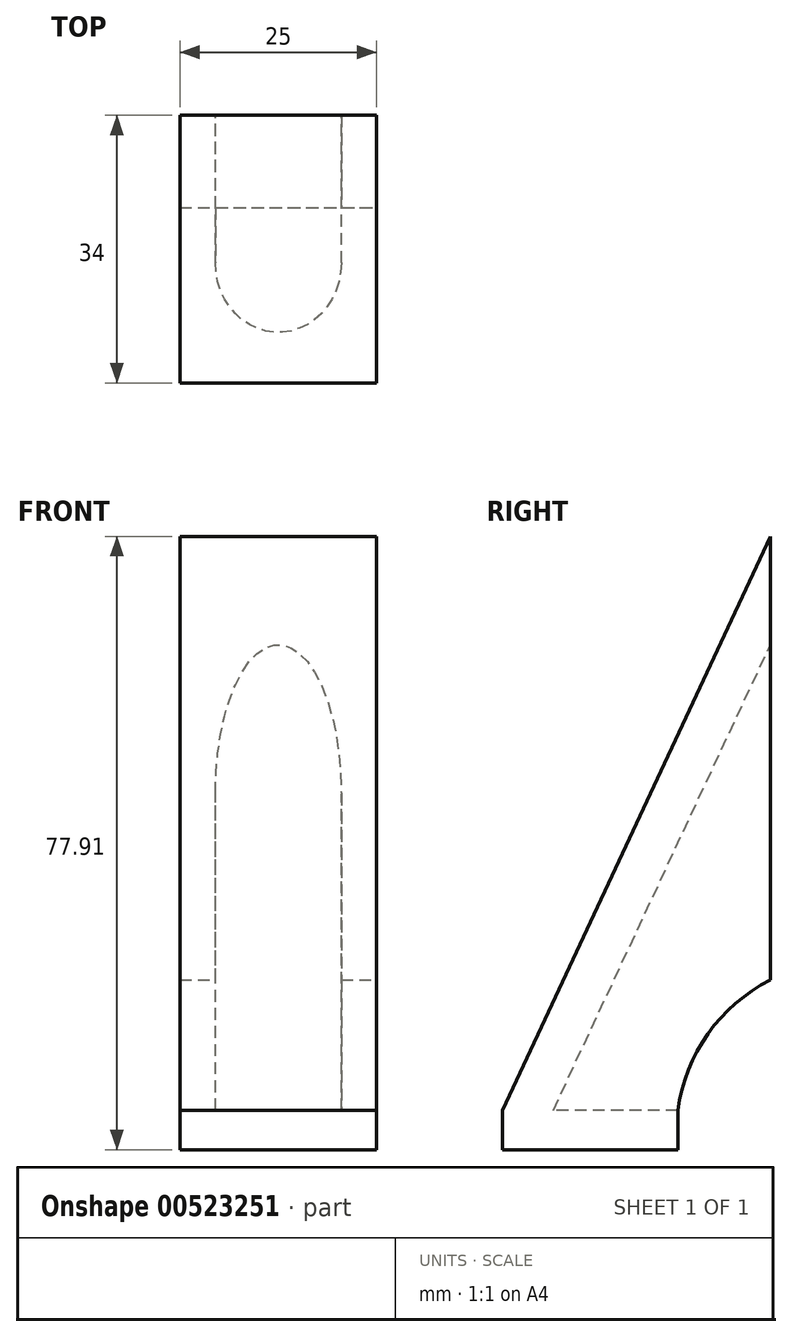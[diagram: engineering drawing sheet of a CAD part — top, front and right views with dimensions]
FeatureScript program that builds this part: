
annotation { "Feature Type Name" : "Feature", "Feature Type Description" : "" }
export const myFeature = defineFeature(function(context is Context, id is Id, definition is map)
    precondition{}
    {
        {
            var Q0;
            Q0=qCreatedBy(makeId("Right.planeOp"),FACE);
            var sketch = newSketch(context, id + "F0", { "sketchPlane" : qUnion([Q0])});
            skLineSegment(sketch, "E0", {"start": v(0, 0) * mm, "end": v(-34, 0) * mm});
            skLineSegment(sketch, "E1", {"start": v(-34, 0) * mm, "end": v(0, 72.91) * mm});
            skLineSegment(sketch, "E2", {"start": v(0, 72.91) * mm, "end": v(0, 0) * mm});
            skSolve(sketch);
        }
        {
            var Q0;
            Q0 = qSketchRegion(id + "F0", true);
            extrude(context, id + "F1", {"entities" : qUnion([Q0]), "depth" : 25 * mm, "offsetDistance" : 25.4 * mm, "symmetric" : true});
        }
        {
            var Q0;
            Q0=makeQuery(id+"F1.opExtrude","CAP_VERTEX",VERTEX,{"disambiguationData":[OSD([sQuery(id+"F0.wireOp",EDGE,"E1"),sQuery(id+"F0.wireOp",EDGE,"E2")])],"isStart":false});
            var Q1;
            Q1=makeQuery(id+"F1.opExtrude","CAP_EDGE",EDGE,{"disambiguationData":[OSD([sQuery(id+"F0.wireOp",EDGE,"E1")])],"isStart":false});
            cPlane(context, id + "F2", {"entities" : qUnion([Q0, Q1]), "cplaneType" : CPlaneType.LINE_POINT, "offset" : 25 * mm, "width" : 150 * mm, "height" : 150 * mm});
        }
        {
            var Q0;
            Q0=qCreatedBy(makeId("Right.planeOp"),FACE);
            var sketch = newSketch(context, id + "F3", { "sketchPlane" : qUnion([Q0])});
            skLineSegment(sketch, "E3", {"start": v(-11.76, 0) * mm, "end": v(0, 0) * mm});
            skLineSegment(sketch, "E4", {"start": v(0, 0) * mm, "end": v(0, 16.54) * mm});
            skArc(sketch, "E5", {"start": v(0, 16.54) * mm, "mid": v(-7.92, 9.72) * mm, "end": v(-11.76, 0) * mm});
            skSolve(sketch);
        }
        {
            var Q0;
            Q0 = qSketchRegion(id + "F3", true);
            extrude(context, id + "F4", {"entities" : qUnion([Q0]), "operationType" : NewBodyOperationType.REMOVE, "endBound" : BoundingType.UP_TO_NEXT, "oppositeDirection" : true, "depth" : 250 * mm, "offsetDistance" : 25 * mm, "hasSecondDirection" : true, "secondDirectionBound" : BoundingType.UP_TO_NEXT, "secondDirectionOppositeDirection" : false, "secondDirectionDepth" : 25 * mm});
        }
        {
            var Q0;
            Q0=qCreatedBy(id+"F2.planeOp",FACE);
            var sketch = newSketch(context, id + "F5", { "sketchPlane" : qUnion([Q0])});
            skArc(sketch, "E6", {"start": v(-8, -17) * mm, "mid": v(0, -25) * mm, "end": v(8, -17) * mm});
            skLineSegment(sketch, "E7", {"start": v(8, -17) * mm, "end": v(8, 3.53) * mm});
            skLineSegment(sketch, "E8", {"start": v(8, 3.53) * mm, "end": v(-8, 3.53) * mm});
            skLineSegment(sketch, "E9", {"start": v(-8, 3.53) * mm, "end": v(-8, -17) * mm});
            skSolve(sketch);
        }
        {
            var Q0;
            Q0 = qSketchRegion(id + "F5", true);
            var Q1;
            Q1=makeQuery(id+"F1.opExtrude","SWEPT_FACE",FACE,{"disambiguationData":[OSD([sQuery(id+"F0.wireOp",EDGE,"E0")])]});
            extrude(context, id + "F6", {"entities" : qUnion([Q0]), "operationType" : NewBodyOperationType.REMOVE, "endBound" : BoundingType.UP_TO_SURFACE, "oppositeDirection" : true, "depth" : 25 * mm, "endBoundEntityFace" : qUnion([Q1]), "offsetDistance" : 25 * mm});
        }
        {
            var Q0;
            Q0=makeQuery(id+"F1.opExtrude","SWEPT_FACE",FACE,{"disambiguationData":[OSD([sQuery(id+"F0.wireOp",EDGE,"E0")])]});
            var sketch = newSketch(context, id + "F7", { "sketchPlane" : qUnion([Q0])});
            skLineSegment(sketch, "E10.bottom", {"start": v(-12.5, 34) * mm, "end": v(12.5, 34) * mm});
            skLineSegment(sketch, "E10.top", {"start": v(-12.5, 11.76) * mm, "end": v(12.5, 11.76) * mm});
            skLineSegment(sketch, "E10.left", {"start": v(-12.5, 34) * mm, "end": v(-12.5, 11.76) * mm});
            skLineSegment(sketch, "E10.right", {"start": v(12.5, 34) * mm, "end": v(12.5, 11.76) * mm});
            skSolve(sketch);
        }
        {
            var Q0;
            Q0 = qSketchRegion(id + "F7", true);
            extrude(context, id + "F8", {"entities" : qUnion([Q0]), "operationType" : NewBodyOperationType.ADD, "depth" : 5 * mm, "offsetDistance" : 25 * mm});
        }
    });
